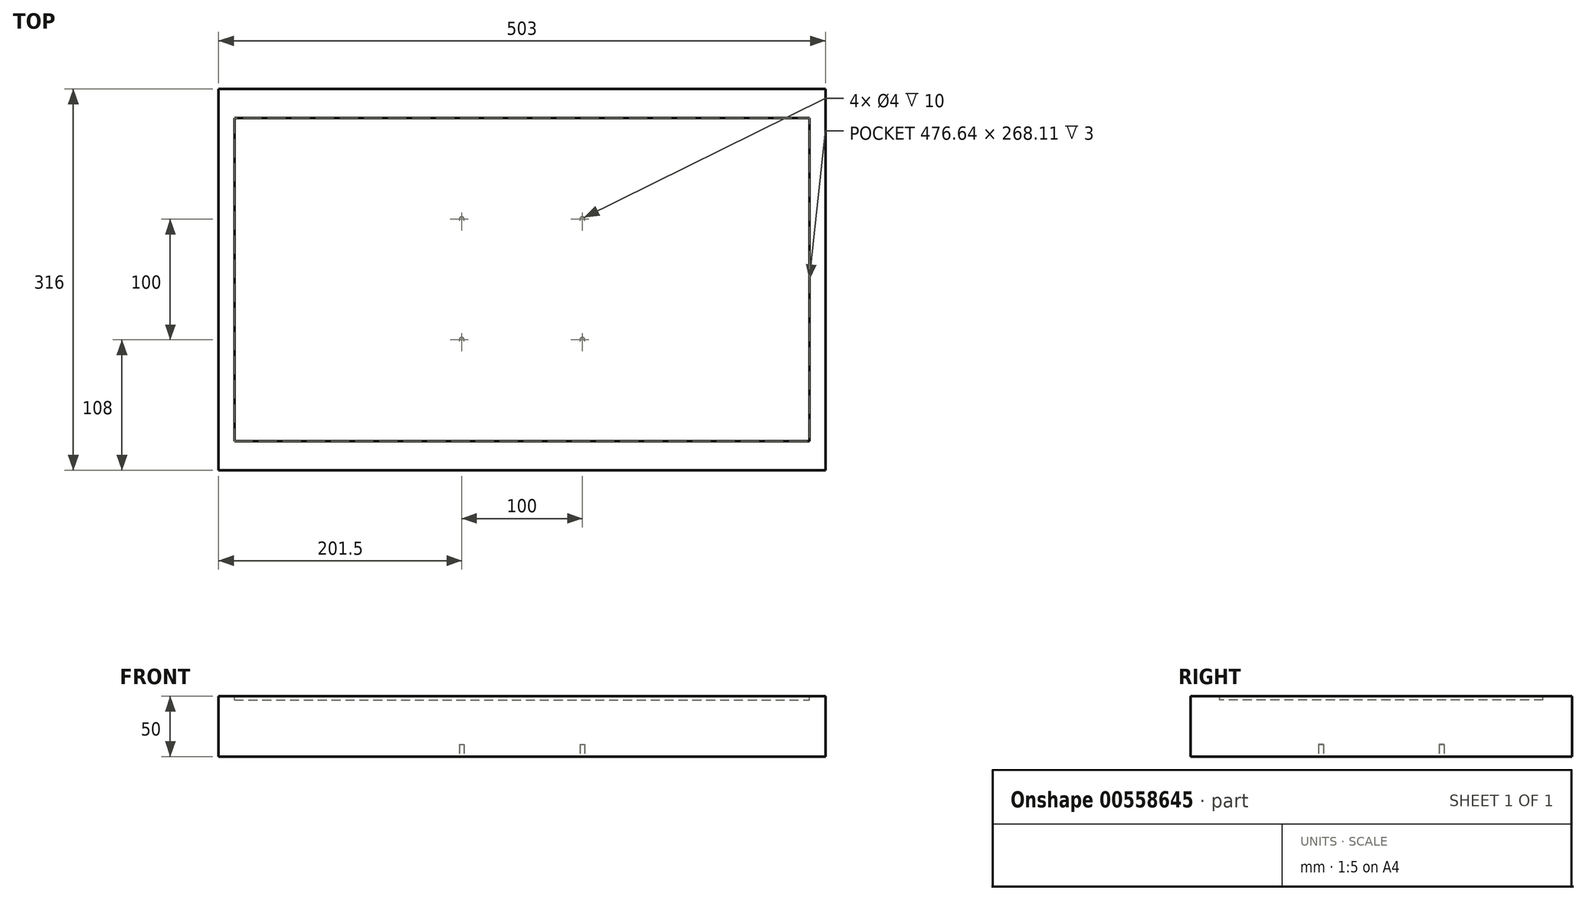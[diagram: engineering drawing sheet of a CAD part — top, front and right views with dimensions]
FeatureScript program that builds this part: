
annotation { "Feature Type Name" : "Feature", "Feature Type Description" : "" }
export const myFeature = defineFeature(function(context is Context, id is Id, definition is map)
    precondition{}
    {
        {
            var Q0;
            Q0=qCreatedBy(makeId("Top.planeOp"),FACE);
            var sketch = newSketch(context, id + "F0", { "sketchPlane" : qUnion([Q0])});
            skLineSegment(sketch, "E0.bottom", {"start": v(0, 0) * mm, "end": v(503, 0) * mm});
            skLineSegment(sketch, "E0.top", {"start": v(0, 316) * mm, "end": v(503, 316) * mm});
            skLineSegment(sketch, "E0.left", {"start": v(0, 0) * mm, "end": v(0, 316) * mm});
            skLineSegment(sketch, "E0.right", {"start": v(503, 0) * mm, "end": v(503, 316) * mm});
            skSolve(sketch);
        }
        {
            var Q0;
            Q0=makeQuery(id+"F0.imprint","IMPRINT",FACE,{"disambiguationData":[TD([[makeQuery(id+"F0.imprint","IMPRINT",EDGE,{"derivedFrom":sQuery(id+"F0.wireOp",EDGE,"E0.bottom")}),1.0]])]});
            extrude(context, id + "F1", {"entities" : qUnion([Q0]), "depth" : 50 * mm, "offsetDistance" : 25 * mm});
        }
        {
            var Q0;
            Q0=makeQuery(id+"F1.opExtrude","CAP_FACE",FACE,{"disambiguationData":[OSD([sQuery(id+"F0.wireOp",EDGE,"E0.bottom"),sQuery(id+"F0.wireOp",EDGE,"E0.top"),sQuery(id+"F0.wireOp",EDGE,"E0.left"),sQuery(id+"F0.wireOp",EDGE,"E0.right")])],"isStart":true});
            var sketch = newSketch(context, id + "F2", { "sketchPlane" : qUnion([Q0])});
            skLineSegment(sketch, "E1.bottom", {"start": v(301.5, -208) * mm, "end": v(201.5, -208) * mm, "construction": true});
            skLineSegment(sketch, "E1.top", {"start": v(301.5, -108) * mm, "end": v(201.5, -108) * mm, "construction": true});
            skLineSegment(sketch, "E1.left", {"start": v(301.5, -208) * mm, "end": v(301.5, -108) * mm, "construction": true});
            skLineSegment(sketch, "E1.right", {"start": v(201.5, -208) * mm, "end": v(201.5, -108) * mm, "construction": true});
            skLineSegment(sketch, "E2", {"start": v(251.5, -316) * mm, "end": v(251.5, -208) * mm, "construction": true});
            skLineSegment(sketch, "E3", {"start": v(503, -158) * mm, "end": v(301.5, -158) * mm, "construction": true});
            skCircle(sketch, "E4", {"center": v(301.5, -208) * mm, "radius": 2 * mm});
            skCircle(sketch, "E5", {"center": v(201.5, -208) * mm, "radius": 2 * mm});
            skCircle(sketch, "E6", {"center": v(201.5, -108) * mm, "radius": 2 * mm});
            skCircle(sketch, "E7", {"center": v(301.5, -108) * mm, "radius": 2 * mm});
            skSolve(sketch);
        }
        {
            var Q0;
            Q0 = qSketchRegion(id + "F2", true);
            extrude(context, id + "F3", {"entities" : qUnion([Q0]), "operationType" : NewBodyOperationType.REMOVE, "oppositeDirection" : true, "depth" : 10 * mm, "offsetDistance" : 25 * mm});
        }
        {
            var Q0;
            Q0=makeQuery(id+"F1.opExtrude","CAP_FACE",FACE,{"disambiguationData":[OSD([sQuery(id+"F0.wireOp",EDGE,"E0.bottom"),sQuery(id+"F0.wireOp",EDGE,"E0.top"),sQuery(id+"F0.wireOp",EDGE,"E0.left"),sQuery(id+"F0.wireOp",EDGE,"E0.right")])],"isStart":false});
            var sketch = newSketch(context, id + "F4", { "sketchPlane" : qUnion([Q0])});
            skLineSegment(sketch, "E8.bottom", {"start": v(13.18, 292.05) * mm, "end": v(489.82, 292.06) * mm});
            skLineSegment(sketch, "E8.top", {"start": v(13.18, 23.95) * mm, "end": v(489.82, 23.95) * mm});
            skLineSegment(sketch, "E8.left", {"start": v(13.18, 292.05) * mm, "end": v(13.18, 23.95) * mm});
            skLineSegment(sketch, "E8.right", {"start": v(489.82, 292.06) * mm, "end": v(489.82, 23.95) * mm});
            skLineSegment(sketch, "E9", {"start": v(0, 158) * mm, "end": v(13.18, 158) * mm, "construction": true});
            skLineSegment(sketch, "E10", {"start": v(251.5, 316) * mm, "end": v(251.5, 292.06) * mm, "construction": true});
            skSolve(sketch);
        }
        {
            var Q0;
            Q0=makeQuery(id+"F4.imprint","IMPRINT",FACE,{"disambiguationData":[TD([[makeQuery(id+"F4.imprint","IMPRINT",EDGE,{"derivedFrom":sQuery(id+"F4.wireOp",EDGE,"E8.bottom")}),-1.0]])]});
            extrude(context, id + "F5", {"entities" : qUnion([Q0]), "operationType" : NewBodyOperationType.REMOVE, "oppositeDirection" : true, "depth" : 3 * mm, "offsetDistance" : 25 * mm});
        }
    });
